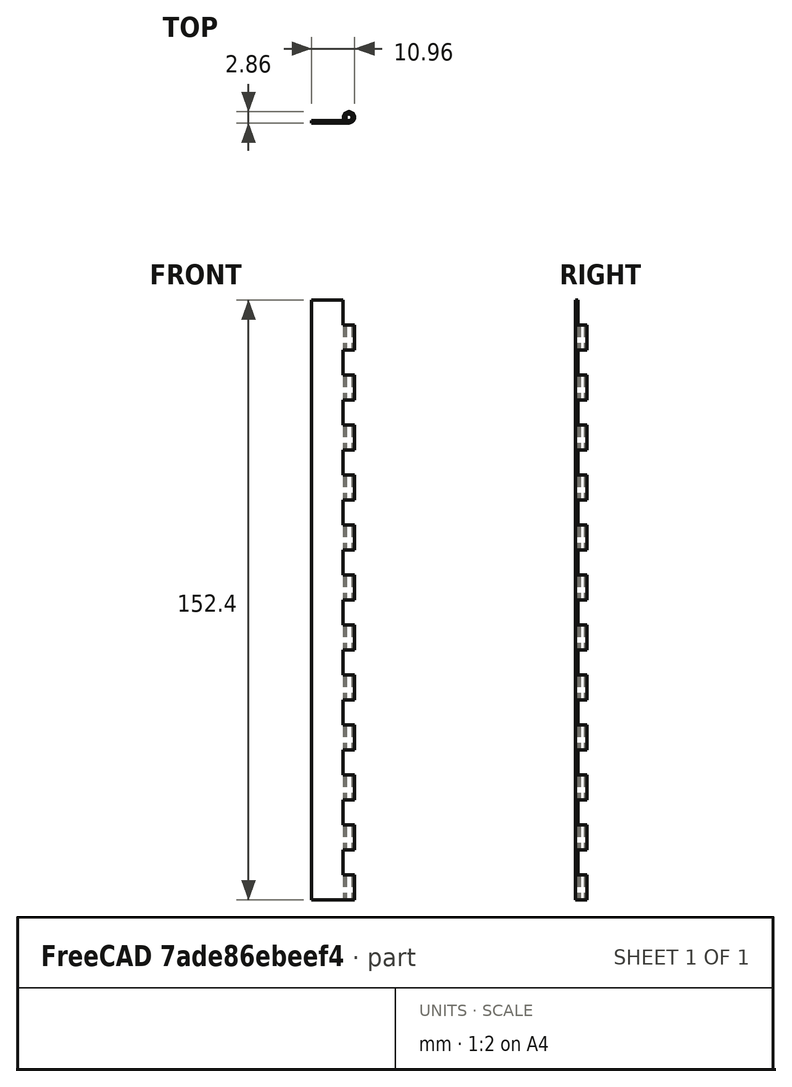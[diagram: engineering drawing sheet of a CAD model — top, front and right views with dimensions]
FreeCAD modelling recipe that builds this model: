
FCSTD DOCUMENT  (FreeCAD 0.19R24267 (Git))
Label: hinge_l-6
License: All rights reserved
LicenseURL: http://en.wikipedia.org/wiki/All_rights_reserved
objects: Part::Feature×1, Sketcher::SketchObject×1, Part::Extrusion×1, Part::Cut×1
note: 4 computed .brp shape members not serialized (recipe doc carries the construction recipe); baked Part::Feature solids carry a one-line shape summary decoded from their .brp

FEATURE [Part::Feature] Solid002
  shape: bbox 10.95 x 2.858 x 304.8 mm, 244 faces (baked)
FEATURE [Sketcher::SketchObject] Sketch
  FullyConstrained = false
  MapMode = 5
  Placement = pos=(0,0,152.4) rot=(0,0,1;0rad)
  Support = -> [Solid002]
  sketch-geometry (4):
    g0: LineSegment StartX=-10.6977 StartY=3.40063 StartZ=0 EndX=3.33717 EndY=3.40063 EndZ=0
    g1: LineSegment StartX=3.33717 StartY=3.40063 StartZ=0 EndX=3.33717 EndY=-2.84486 EndZ=0
    g2: LineSegment StartX=3.33717 StartY=-2.84486 StartZ=0 EndX=-10.6977 EndY=-2.84486 EndZ=0
    g3: LineSegment StartX=-10.6977 StartY=-2.84486 StartZ=0 EndX=-10.6977 EndY=3.40063 EndZ=0
  constraints (8):
    c: Coincident(g0,g1)
    c: Coincident(g1,g2)
    c: Coincident(g2,g3)
    c: Coincident(g3,g0)
    c: Horizontal(g0)
    c: Horizontal(g2)
    c: Vertical(g1)
    c: Vertical(g3)
FEATURE [Part::Extrusion] Extrude
  Base = -> Sketch
  Dir = (0,0,1)
  DirMode = 2
  FaceMakerClass = Part::FaceMakerBullseye
  LengthFwd = 0
  LengthRev = 152.4
  Solid = true
  Symmetric = false
FEATURE [Part::Cut] Cut
  Base = -> Solid002
  Tool = -> Extrude
